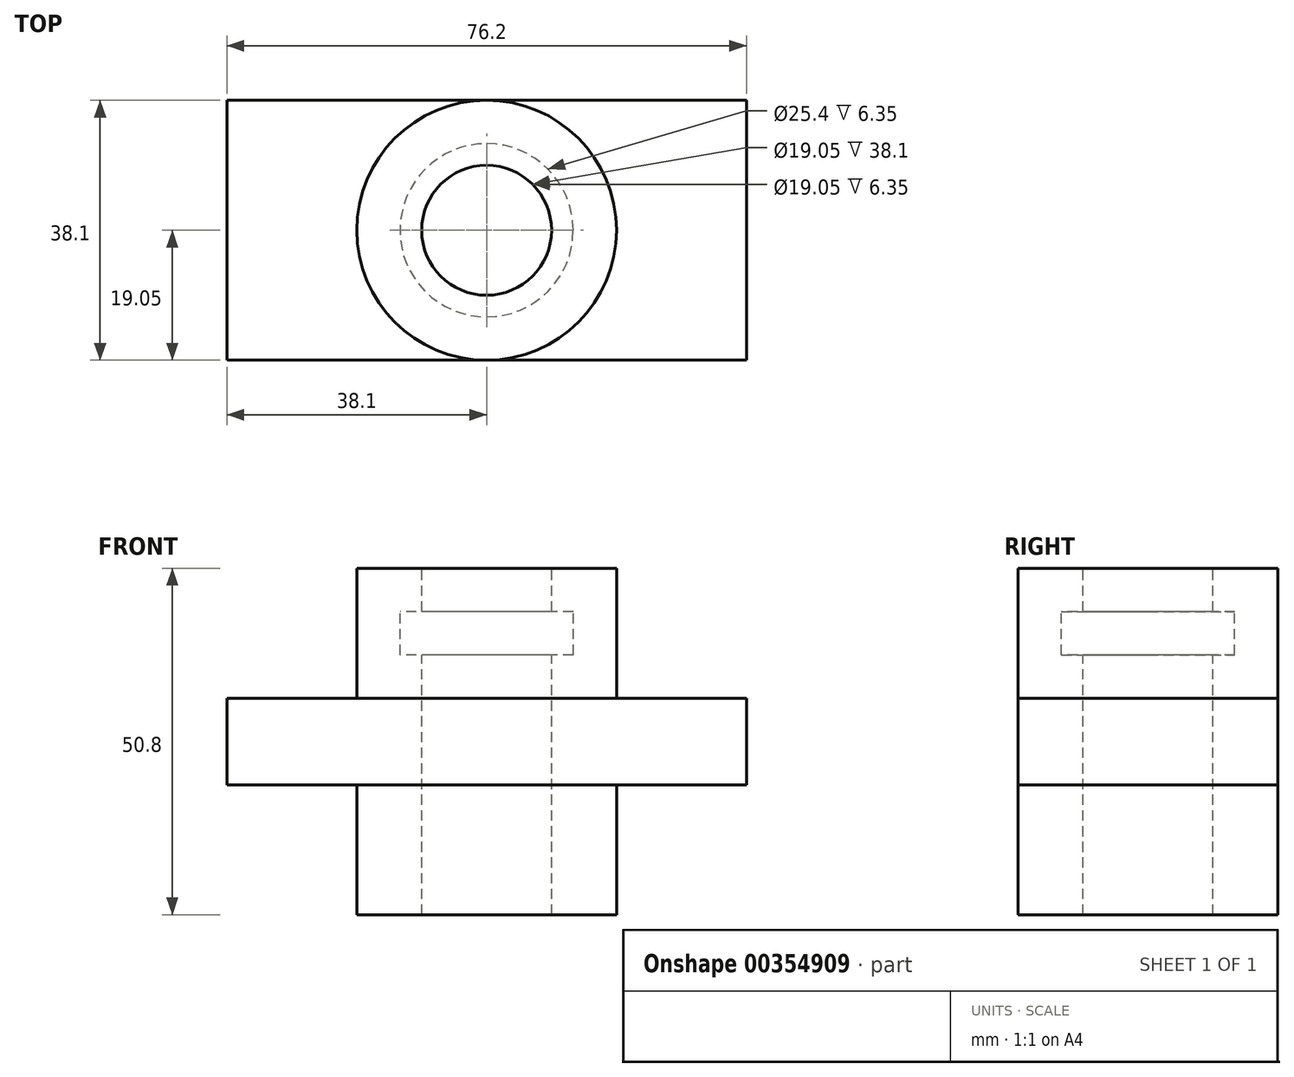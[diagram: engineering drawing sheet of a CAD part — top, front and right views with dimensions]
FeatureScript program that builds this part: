
annotation { "Feature Type Name" : "Feature", "Feature Type Description" : "" }
export const myFeature = defineFeature(function(context is Context, id is Id, definition is map)
    precondition{}
    {
        {
            var Q0;
            Q0=qCreatedBy(makeId("Top.planeOp"),FACE);
            var sketch = newSketch(context, id + "F0", { "sketchPlane" : qUnion([Q0])});
            skLineSegment(sketch, "E0.bottom", {"start": v(38.1, 19.05) * mm, "end": v(-38.1, 19.05) * mm});
            skLineSegment(sketch, "E0.top", {"start": v(38.1, -19.05) * mm, "end": v(-38.1, -19.05) * mm});
            skLineSegment(sketch, "E0.left", {"start": v(38.1, 19.05) * mm, "end": v(38.1, -19.05) * mm});
            skLineSegment(sketch, "E0.right", {"start": v(-38.1, 19.05) * mm, "end": v(-38.1, -19.05) * mm});
            skPoint(sketch, "E0.middle", {"position": v(0, 0) * mm});
            skCircle(sketch, "E1", {"center": v(0, 0) * mm, "radius": 19.05 * mm});
            skSolve(sketch);
        }
        {
            var Q0;
            Q0 = qSketchRegion(id + "F0", true);
            var Q1;
            Q1=makeQuery(id+"F0.imprint","IMPRINT",FACE,{"disambiguationData":[TD([[makeQuery(id+"F0.imprint","IMPRINT",EDGE,{"derivedFrom":sQuery(id+"F0.wireOp",EDGE,"E1")}),1.0]])]});
            extrude(context, id + "F1", {"entities" : qUnion([Q0, Q1]), "endBound" : BoundingType.SYMMETRIC, "depth" : 12.7 * mm});
        }
        {
            var Q0;
            Q0=makeQuery(id+"F0.imprint","IMPRINT",FACE,{"disambiguationData":[TD([[makeQuery(id+"F0.imprint","IMPRINT",EDGE,{"derivedFrom":sQuery(id+"F0.wireOp",EDGE,"E1")}),1.0]])]});
            extrude(context, id + "F2", {"entities" : qUnion([Q0]), "operationType" : NewBodyOperationType.ADD, "endBound" : BoundingType.SYMMETRIC, "depth" : 50.8 * mm});
        }
        {
            var Q0;
            Q0=makeQuery(id+"F2.opExtrude","CAP_FACE",FACE,{"disambiguationData":[OSD([sQuery(id+"F0.wireOp",EDGE,"E1")])],"isStart":false});
            var sketch = newSketch(context, id + "F3", { "sketchPlane" : qUnion([Q0])});
            skCircle(sketch, "E2", {"center": v(0, 0) * mm, "radius": 9.53 * mm});
            skCircle(sketch, "E3", {"center": v(0, 0) * mm, "radius": 12.7 * mm});
            skSolve(sketch);
        }
        {
            var Q0;
            Q0=makeQuery(id+"F3.imprint","IMPRINT",FACE,{"disambiguationData":[TD([[makeQuery(id+"F3.imprint","IMPRINT",EDGE,{"derivedFrom":sQuery(id+"F3.wireOp",EDGE,"E2")}),1.0]])]});
            var Q1;
            Q1=makeQuery(id+"F2.opExtrude","CAP_FACE",FACE,{"disambiguationData":[OSD([sQuery(id+"F0.wireOp",EDGE,"E1")])],"isStart":true});
            extrude(context, id + "F4", {"entities" : qUnion([Q0]), "operationType" : NewBodyOperationType.REMOVE, "endBound" : BoundingType.UP_TO_SURFACE, "oppositeDirection" : true, "endBoundEntityFace" : qUnion([Q1]), "depth" : 25.4 * mm});
        }
        {
            var Q0;
            Q0=makeQuery(id+"F3.imprint","IMPRINT",FACE,{"disambiguationData":[TD([[makeQuery(id+"F3.imprint","IMPRINT",EDGE,{"derivedFrom":sQuery(id+"F3.wireOp",EDGE,"E2")}),-1.0]])]});
            extrude(context, id + "F5", {"entities" : qUnion([Q0]), "operationType" : NewBodyOperationType.REMOVE, "oppositeDirection" : true, "depth" : 12.7 * mm});
        }
        {
            var Q0;
            Q0=makeQuery(id+"F3.imprint","IMPRINT",FACE,{"disambiguationData":[TD([[makeQuery(id+"F3.imprint","IMPRINT",EDGE,{"derivedFrom":sQuery(id+"F3.wireOp",EDGE,"E2")}),-1.0]])]});
            extrude(context, id + "F6", {"entities" : qUnion([Q0]), "operationType" : NewBodyOperationType.ADD, "oppositeDirection" : true, "depth" : 6.35 * mm});
        }
    });
